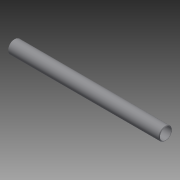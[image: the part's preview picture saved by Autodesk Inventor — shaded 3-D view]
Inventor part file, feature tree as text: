
AUTODESK INVENTOR PART (.ipt)
format: ipt  version: 2014 SP2 (Build 180246200, 246)  size: 129,024 bytes
history: native  units: in
note: dims shown in document units (in); Inventor stores cm internally (conversion verified against a paired STEP export)
features: other x42, revolve x1, sketch x1
ambient origin geometry x8: Origin, YZ Plane, XZ Plane, XY Plane, X Axis, Y Axis, Z Axis, Center Point
bodies: Solid1 (feature_tree)
feature tree (44):
  revolve  "Revolution1"  [1 undecoded]
  other  "cp1_XY"
  other  "cp1_YZ"
  other  "cp1_ZX"
  other  "cp1_X"
  other  "cp1_Y"
  other  "cp1_Z"
  other  "cp1_Center"
  other  "cp2_XY"
  other  "cp2_YZ"
  other  "cp2_ZX"
  other  "cp2_X"
  other  "cp2_Y"
  other  "cp2_Z"
  other  "cp2_Center"
  other  "cp3_XY"
  other  "cp3_YZ"
  other  "cp3_ZX"
  other  "cp3_X"
  other  "cp3_Y"
  other  "cp3_Z"
  other  "cp3_Center"
  other  "cp4_XY"
  other  "cp4_YZ"
  other  "cp4_ZX"
  other  "cp4_X"
  other  "cp4_Y"
  other  "cp4_Z"
  other  "cp4_Center"
  other  "tube_front_XY"
  other  "tube_front_YZ"
  other  "tube_front_ZX"
  other  "tube_front_X"
  other  "tube_front_Y"
  other  "tube_front_Z"
  other  "tube_front_Center"
  other  "tube_rear_XY"
  other  "tube_rear_YZ"
  other  "tube_rear_ZX"
  other  "tube_rear_X"
  other  "tube_rear_Y"
  other  "tube_rear_Z"
  other  "tube_rear_Center"
  sketch  "Sketch_1"  dims[d0=360.0deg]
note: 1 required parameter value undecoded (feature->parameter linkage not recoverable at this tier; creation-order binding heuristic only, values carry confidence <= 0.55)
